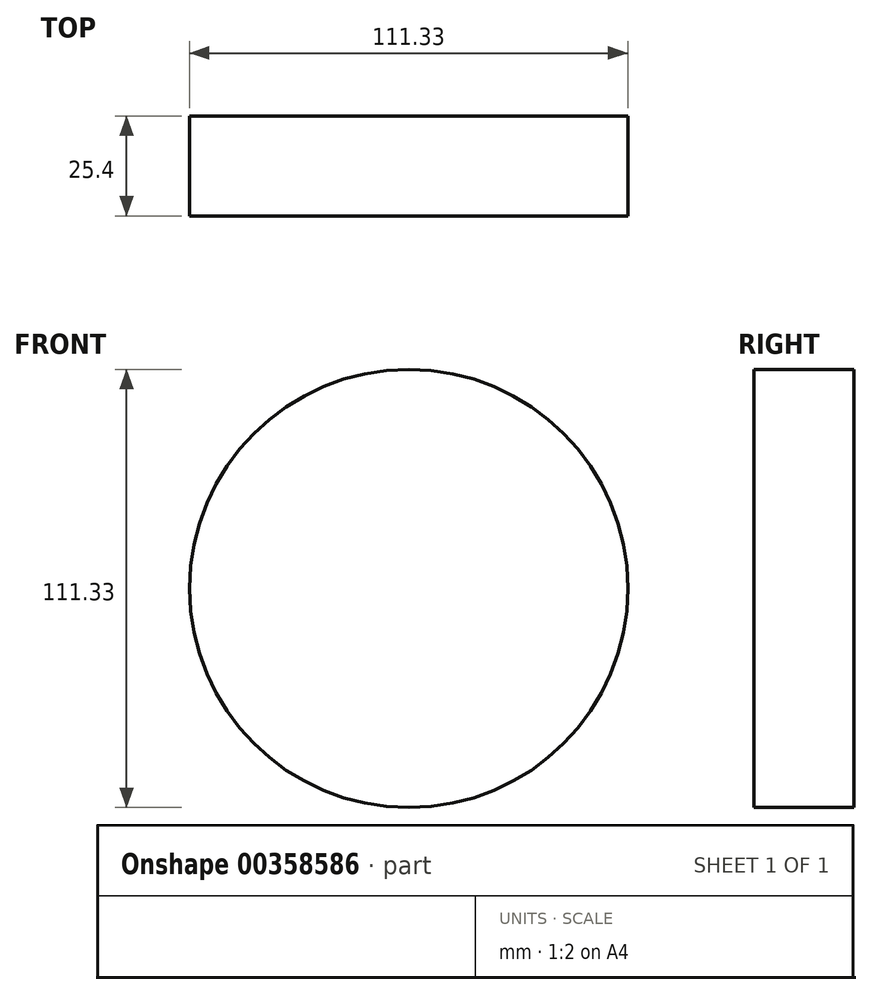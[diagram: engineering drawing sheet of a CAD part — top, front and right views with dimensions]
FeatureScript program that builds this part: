
annotation { "Feature Type Name" : "Feature", "Feature Type Description" : "" }
export const myFeature = defineFeature(function(context is Context, id is Id, definition is map)
    precondition{}
    {
        {
            var Q0;
            Q0=qCreatedBy(makeId("Front.planeOp"),FACE);
            var sketch = newSketch(context, id + "F0", { "sketchPlane" : qUnion([Q0])});
            skCircle(sketch, "E0", {"center": v(-22.3, 10.48) * mm, "radius": 55.66 * mm});
            skSolve(sketch);
        }
        {
            var Q0;
            Q0 = qSketchRegion(id + "F0", true);
            extrude(context, id + "F1", {"entities" : qUnion([Q0]), "depth" : 25.4 * mm});
        }
    });
